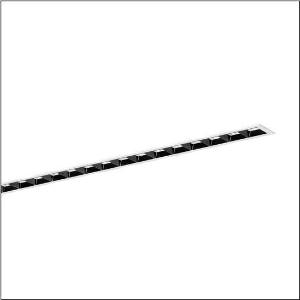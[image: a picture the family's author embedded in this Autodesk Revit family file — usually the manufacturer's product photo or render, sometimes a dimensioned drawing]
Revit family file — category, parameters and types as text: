
# Revit family: silica_r__21_51mx11db45wb_df67
name_source: partatom
category: Lighting Fixtures
units: mm (PartAtom-declared; Revit-internal decimal feet)

## family parameters
Cut with Voids When Loaded = No
Host = Face
Light Source = No
Part Type = Normal
Room Calculation Point = No
Round Connector Dimension = Use Diameter
Shared = No

## types (1)
- --- (1 x LED, 5400 lm, 32 W, 4000K)
    Apparent Load = 32 VA
    CIE Flux Codes = 87 99 100 100 100
    Color Rendering = 80
    Color Temperature = 4000K
    Default Elevation = 1800 mm
    Description = Silica® 21, office luminaire, primary light control with darklight reflector, of PMMA, black, CAT 2 (L<= 3000cd/m²), light emission: direct distribution, primary light characteristic: symmetric, installation type: recessed, LED, rated luminous flux: 5.400lm, luminous efficacy: 169lm/W, light colour: 840, colour temperature: 4000K, with terminal, 3+2-pole, max. 2.5mm², mains connection: 220..240V, AC, 50/60Hz, rated input power: 32W, luminaire housing, of aluminium, traffic white (RAL 9016), length: 1.528mm, width: 79mm, height: 53mm, protection rating (complete): IP20, insulation class (complete): insulation class I (protective earthing), certification: CE, permissible operating ambient temperature: 0..+35°C, standard: EN 50419, packaging unit: 1 piece
    Height = 0 mm  [stored 0 ft]
    Lamp = 1 x LED
    Lamp Light Flux = 5400 lm
    Lamp Power = 32 W
    Lamp count = 1
    Length = 1527 mm
    Luminous efficacy = 169 lm/W
    Manufacturer = Siteco
    ModVariant = No
    Model = 51MX11DB45WB
    Mounting Place = Ceiling
    Mounting Type = Recessed
    Number of Poles = 1
    OnlyDefault = Yes
    Power Factor = 1
    Product Name = Silica® 21
    Product group = office luminaire | ceiling recessed
    ProductGroupID = 401
    Protection Class = Protection class I
    Protection Degree = IP 20
    RLX_Detail_Level = 1
    RLX_Emergency_Light_Flux = 0 lm
    RLX_Emergency_Type = 0
    RLX_Emergency_Type_DB = No
    RlxData = <blob elided: 42409 chars, md5=be45edff>
    Socket = socket
    Standby Power = 0 W
    System Light Flux = 5400 lm
    System Power = 32 W
    Type Comments = factory setting: luminous flux: 100 % | dim-lin: 254 | 367 mA
    Type Image = l_1297791.jpg
    URL = http://relux.com
    VarID = @adj_054149
    Voltage = 0 V
    Weight = 0.00 kg
    Width = 79 mm

note: [stored X ft] marks values corroborated as IEEE doubles in the binary element streams (Revit-internal decimal feet)

## geometry (parser evidence)
native form markers: Blend x4, Sweep x10
no freeform markers — native parametric forms only
